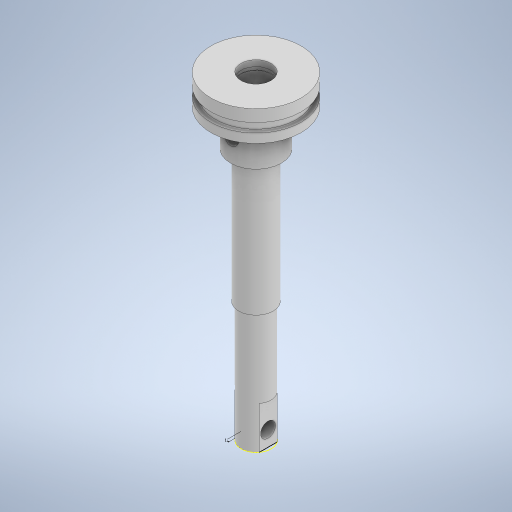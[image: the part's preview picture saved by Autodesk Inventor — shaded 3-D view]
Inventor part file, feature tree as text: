
AUTODESK INVENTOR PART (.ipt)
format: ipt  version: 2023 (Build 270158000, 158)  size: 327,168 bytes
history: native  units: mm
features: sketch x4, extrude x2, revolve x1, hole x1
ambient origin geometry x8: Origin, YZ Plane, XZ Plane, XY Plane, X Axis, Y Axis, Z Axis, Center Point
bodies: Solido1 (feature_tree)
feature tree (8):
  revolve  "Rivoluzione1"
  extrude  "Estrusione1"  Depth=10.0mm
  extrude  "Estrusione2"  Depth=11.5mm
  hole  "Foro1"  [1 undecoded]
  sketch  "Schizzo1"
  sketch  "Schizzo2"
  sketch  "Schizzo3"
  sketch  "Schizzo4"
note: 1 required parameter value undecoded (feature->parameter linkage not recoverable at this tier; creation-order binding heuristic only, values carry confidence <= 0.55)
